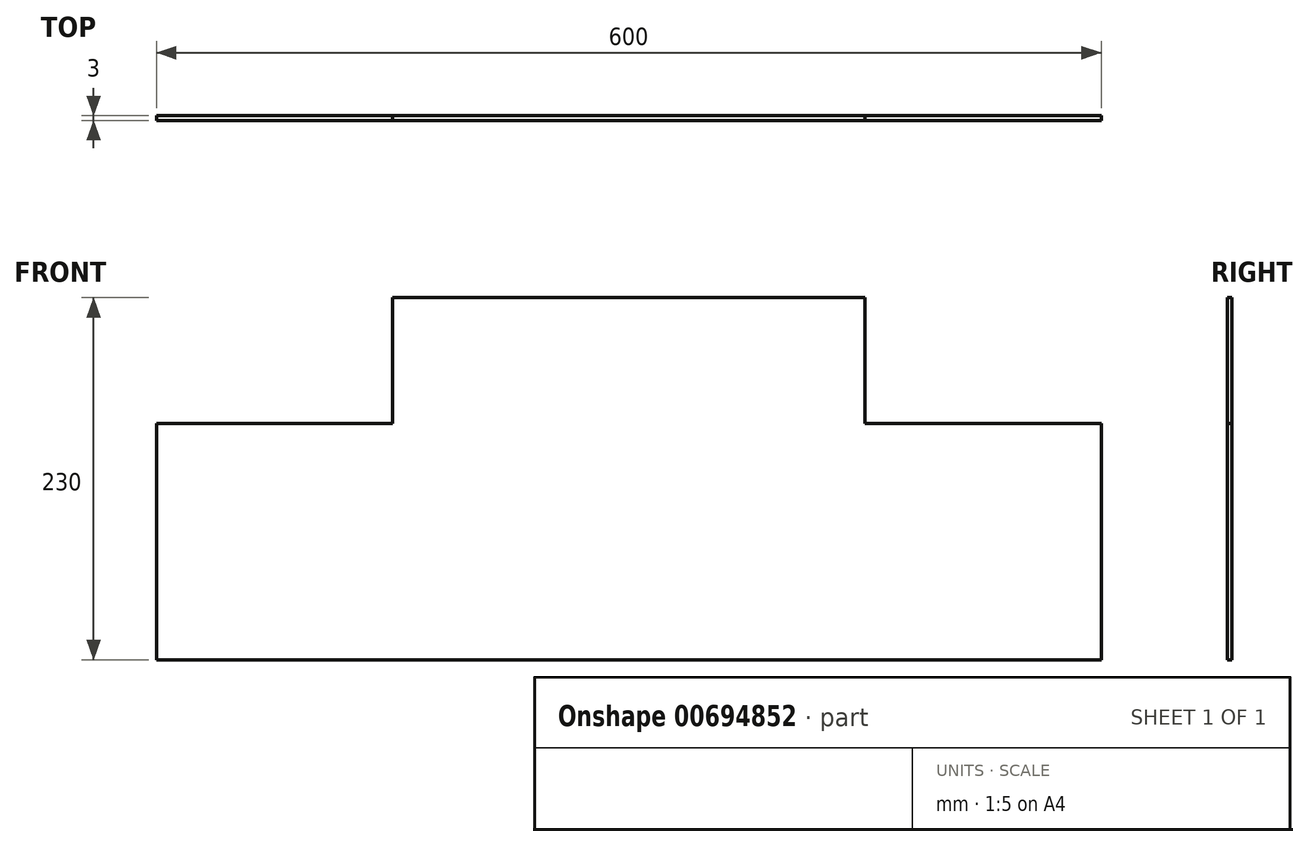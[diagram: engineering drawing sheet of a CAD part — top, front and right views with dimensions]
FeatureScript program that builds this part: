
annotation { "Feature Type Name" : "Feature", "Feature Type Description" : "" }
export const myFeature = defineFeature(function(context is Context, id is Id, definition is map)
    precondition{}
    {
        {
            var Q0;
            Q0=qCreatedBy(makeId("Front.planeOp"),FACE);
            var sketch = newSketch(context, id + "F0", { "sketchPlane" : qUnion([Q0])});
            skLineSegment(sketch, "E0.bottom", {"start": v(300, 115) * mm, "end": v(-300, 115) * mm});
            skLineSegment(sketch, "E0.top", {"start": v(300, -115) * mm, "end": v(-300, -115) * mm});
            skLineSegment(sketch, "E0.left", {"start": v(300, 115) * mm, "end": v(300, -115) * mm});
            skLineSegment(sketch, "E0.right", {"start": v(-300, 115) * mm, "end": v(-300, -115) * mm});
            skPoint(sketch, "E0.middle", {"position": v(0, 0) * mm});
            skSolve(sketch);
        }
        {
            var Q0;
            Q0 = qSketchRegion(id + "F0", true);
            extrude(context, id + "F1", {"entities" : qUnion([Q0]), "depth" : 3 * mm, "offsetDistance" : 25 * mm});
        }
        {
            var Q0;
            Q0=makeQuery(id+"F1.opExtrude","CAP_FACE",FACE,{"disambiguationData":[OSD([sQuery(id+"F0.wireOp",EDGE,"E0.bottom"),sQuery(id+"F0.wireOp",EDGE,"E0.top"),sQuery(id+"F0.wireOp",EDGE,"E0.left"),sQuery(id+"F0.wireOp",EDGE,"E0.right")])],"isStart":false});
            var sketch = newSketch(context, id + "F2", { "sketchPlane" : qUnion([Q0])});
            skLineSegment(sketch, "E1.bottom", {"start": v(-300, 115) * mm, "end": v(-150, 115) * mm});
            skLineSegment(sketch, "E1.top", {"start": v(-300, 35) * mm, "end": v(-150, 35) * mm});
            skLineSegment(sketch, "E1.left", {"start": v(-300, 115) * mm, "end": v(-300, 35) * mm});
            skLineSegment(sketch, "E1.right", {"start": v(-150, 115) * mm, "end": v(-150, 35) * mm});
            skSolve(sketch);
        }
        {
            var Q0;
            Q0 = qSketchRegion(id + "F2", true);
            extrude(context, id + "F3", {"entities" : qUnion([Q0]), "operationType" : NewBodyOperationType.REMOVE, "endBound" : BoundingType.THROUGH_ALL, "oppositeDirection" : true, "depth" : 25 * mm, "offsetDistance" : 25 * mm});
        }
        {
            var Q0;
            Q0=makeQuery(id+"F1.opExtrude","CAP_FACE",FACE,{"disambiguationData":[OSD([sQuery(id+"F0.wireOp",EDGE,"E0.bottom"),sQuery(id+"F0.wireOp",EDGE,"E0.top"),sQuery(id+"F0.wireOp",EDGE,"E0.left"),sQuery(id+"F0.wireOp",EDGE,"E0.right")])],"isStart":false});
            var sketch = newSketch(context, id + "F4", { "sketchPlane" : qUnion([Q0])});
            skLineSegment(sketch, "E2.bottom", {"start": v(300, 115) * mm, "end": v(150, 115) * mm});
            skLineSegment(sketch, "E2.top", {"start": v(300, 35) * mm, "end": v(150, 35) * mm});
            skLineSegment(sketch, "E2.left", {"start": v(300, 115) * mm, "end": v(300, 35) * mm});
            skLineSegment(sketch, "E2.right", {"start": v(150, 115) * mm, "end": v(150, 35) * mm});
            skSolve(sketch);
        }
        {
            var Q0;
            Q0 = qSketchRegion(id + "F4", true);
            extrude(context, id + "F5", {"entities" : qUnion([Q0]), "operationType" : NewBodyOperationType.REMOVE, "endBound" : BoundingType.THROUGH_ALL, "oppositeDirection" : true, "depth" : 25 * mm, "offsetDistance" : 25 * mm});
        }
        {
            var Q0;
            Q0=makeQuery(id+"F1.opExtrude","CAP_FACE",FACE,{"disambiguationData":[OSD([sQuery(id+"F0.wireOp",EDGE,"E0.bottom"),sQuery(id+"F0.wireOp",EDGE,"E0.top"),sQuery(id+"F0.wireOp",EDGE,"E0.left"),sQuery(id+"F0.wireOp",EDGE,"E0.right")])],"isStart":false});
            var sketch = newSketch(context, id + "F6", { "sketchPlane" : qUnion([Q0])});
            skLineSegment(sketch, "E3", {"start": v(0, 131.31) * mm, "end": v(0, -145.96) * mm, "construction": true});
            skPoint(sketch, "E3.endSnap0", {"position": v(0, -115) * mm});
            skSolve(sketch);
        }
    });
